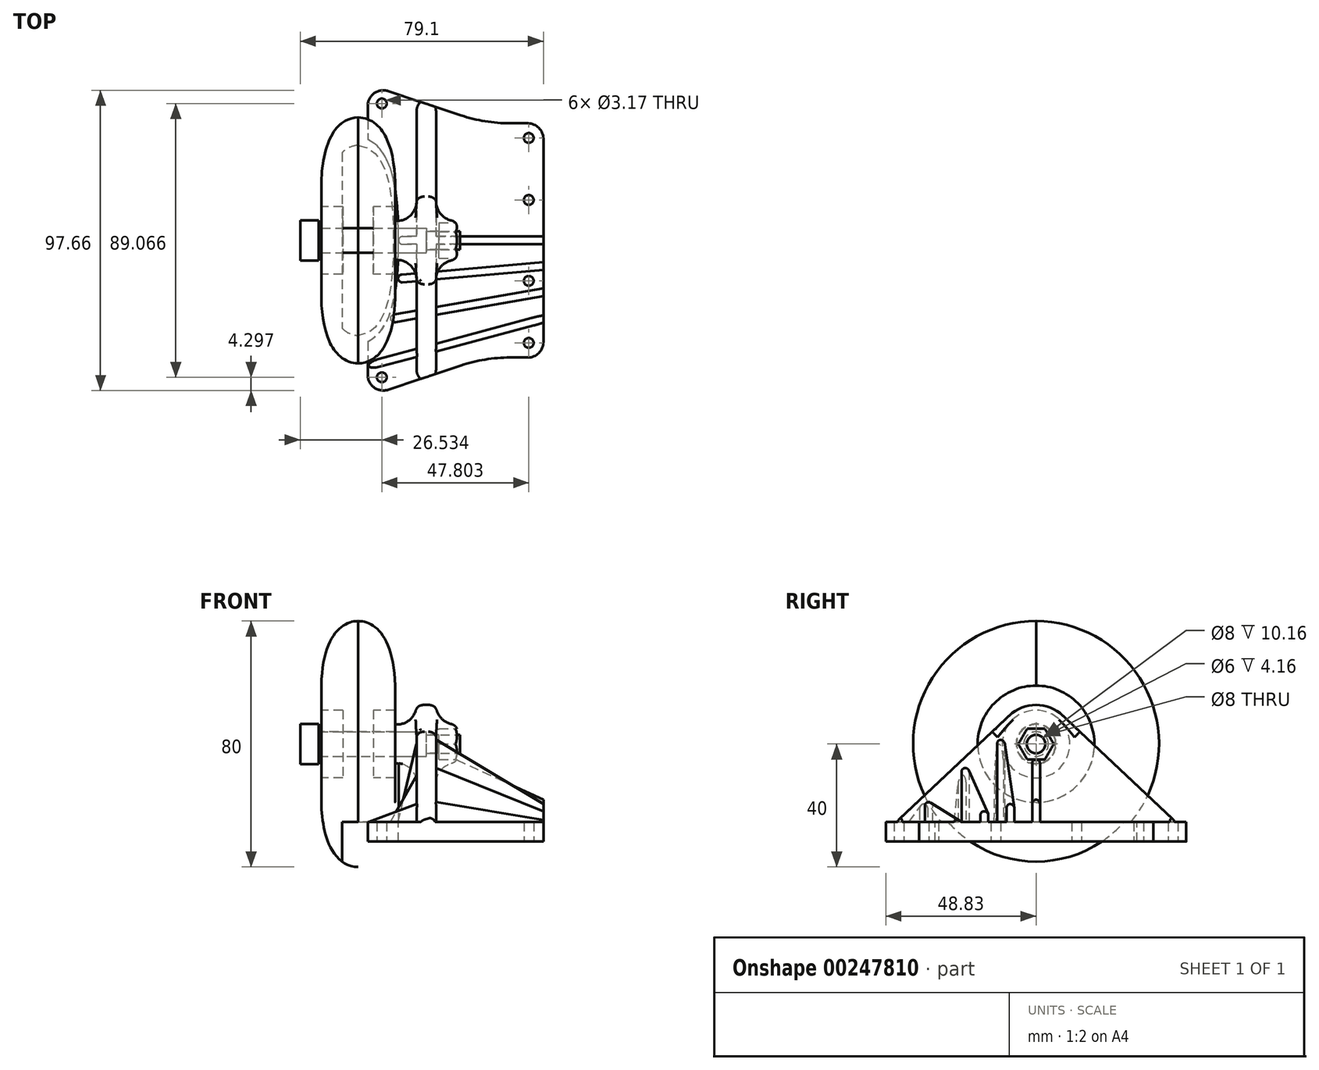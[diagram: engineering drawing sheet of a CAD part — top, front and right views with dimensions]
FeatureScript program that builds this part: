
annotation { "Feature Type Name" : "Feature", "Feature Type Description" : "" }
export const myFeature = defineFeature(function(context is Context, id is Id, definition is map)
    precondition{}
    {
        {
            var Q0;
            Q0=qCreatedBy(makeId("Top.planeOp"),FACE);
            var sketch = newSketch(context, id + "F0", { "sketchPlane" : qUnion([Q0])});
            skLineSegment(sketch, "E0", {"start": v(-19.05, 50.8) * mm, "end": v(-19.05, -50.8) * mm});
            skLineSegment(sketch, "E1", {"start": v(-19.05, -50.8) * mm, "end": v(19.05, -38.1) * mm});
            skLineSegment(sketch, "E2", {"start": v(38.1, -31.75) * mm, "end": v(38.1, 31.75) * mm});
            skLineSegment(sketch, "E3", {"start": v(19.05, 38.1) * mm, "end": v(-19.05, 50.8) * mm});
            skLineSegment(sketch, "E4", {"start": v(19.05, 38.1) * mm, "end": v(38.1, 38.1) * mm});
            skLineSegment(sketch, "E5", {"start": v(38.1, 38.1) * mm, "end": v(38.1, 31.75) * mm});
            skLineSegment(sketch, "E6", {"start": v(19.05, -38.1) * mm, "end": v(38.1, -38.1) * mm});
            skLineSegment(sketch, "E7", {"start": v(38.1, -38.1) * mm, "end": v(38.1, -31.75) * mm});
            skSolve(sketch);
        }
        {
            var Q0;
            Q0=makeQuery(id+"F0.imprint","IMPRINT",FACE,{"disambiguationData":[TD([[makeQuery(id+"F0.imprint","IMPRINT",EDGE,{"derivedFrom":sQuery(id+"F0.wireOp",EDGE,"E0")}),1.0]])]});
            extrude(context, id + "F1", {"entities" : qUnion([Q0]), "depth" : 6.35 * mm});
        }
        {
            var Q0;
            Q0=makeQuery(id+"F1.opExtrude","CAP_FACE",FACE,{"disambiguationData":[OSD([sQuery(id+"F0.wireOp",EDGE,"E0"),sQuery(id+"F0.wireOp",EDGE,"E1"),sQuery(id+"F0.wireOp",EDGE,"E2"),sQuery(id+"F0.wireOp",EDGE,"E3")])],"isStart":false});
            var sketch = newSketch(context, id + "F2", { "sketchPlane" : qUnion([Q0])});
            skLineSegment(sketch, "E8", {"start": v(-3.18, 45.5) * mm, "end": v(-3.17, -45.5) * mm});
            skLineSegment(sketch, "E9", {"start": v(-3.17, -45.5) * mm, "end": v(3.18, -43.4) * mm});
            skLineSegment(sketch, "E10", {"start": v(3.18, -43.4) * mm, "end": v(3.17, 43.4) * mm});
            skLineSegment(sketch, "E11", {"start": v(3.17, 43.4) * mm, "end": v(-3.18, 45.5) * mm});
            skSolve(sketch);
        }
        {
            var Q0;
            Q0=makeQuery(id+"F2.imprint","IMPRINT",FACE,{"disambiguationData":[TD([[makeQuery(id+"F2.imprint","IMPRINT",EDGE,{"derivedFrom":sQuery(id+"F2.wireOp",EDGE,"E8")}),1.0]])]});
            extrude(context, id + "F3", {"entities" : qUnion([Q0]), "operationType" : NewBodyOperationType.ADD, "depth" : 38.1 * mm});
        }
        {
            var Q0;
            Q0=qCreatedBy(makeId("Right.planeOp"),FACE);
            var sketch = newSketch(context, id + "F4", { "sketchPlane" : qUnion([Q0])});
            skArc(sketch, "E12", {"start": v(8.7, 41) * mm, "mid": v(0, 44.45) * mm, "end": v(-8.7, 41) * mm});
            skLineSegment(sketch, "E13", {"start": v(8.7, 41) * mm, "end": v(45.5, 6.35) * mm});
            skLineSegment(sketch, "E14", {"start": v(-8.7, 41) * mm, "end": v(-45.5, 6.35) * mm});
            skLineSegment(sketch, "E15", {"start": v(45.5, 6.35) * mm, "end": v(53.44, 6.35) * mm});
            skLineSegment(sketch, "E16", {"start": v(53.44, 6.35) * mm, "end": v(53.44, 49.76) * mm});
            skLineSegment(sketch, "E17", {"start": v(53.44, 49.76) * mm, "end": v(-55.67, 49.76) * mm});
            skLineSegment(sketch, "E18", {"start": v(-55.67, 49.76) * mm, "end": v(-55.67, 6.35) * mm});
            skLineSegment(sketch, "E19", {"start": v(-55.67, 6.35) * mm, "end": v(-45.5, 6.35) * mm});
            skSolve(sketch);
        }
        {
            var Q0;
            Q0=makeQuery(id+"F4.imprint","IMPRINT",FACE,{"disambiguationData":[TD([[makeQuery(id+"F4.imprint","IMPRINT",EDGE,{"derivedFrom":sQuery(id+"F4.wireOp",EDGE,"E12")}),-1.0]])]});
            extrude(context, id + "F5", {"entities" : qUnion([Q0]), "operationType" : NewBodyOperationType.REMOVE, "oppositeDirection" : true, "depth" : 7.11 * mm, "hasSecondDirection" : true, "secondDirectionOppositeDirection" : false, "secondDirectionDepth" : 4.06 * mm});
        }
        {
            var Q0;
            Q0=qCreatedBy(makeId("Right.planeOp"),FACE);
            var sketch = newSketch(context, id + "F6", { "sketchPlane" : qUnion([Q0])});
            skCircle(sketch, "E20", {"center": v(0, 513) * mm, "radius": 63.5 * mm});
            skCircle(sketch, "E21", {"center": v(0, 31.75) * mm, "radius": 6.35 * mm});
            skSolve(sketch);
        }
        {
            var Q0;
            Q0 = qSketchRegion(id + "F6", true);
            extrude(context, id + "F7", {"entities" : qUnion([Q0]), "operationType" : NewBodyOperationType.ADD, "depth" : 10.16 * mm, "hasSecondDirection" : true, "secondDirectionOppositeDirection" : true, "secondDirectionDepth" : 10.16 * mm});
        }
        {
            var Q0;
            Q0=makeQuery(id+"F7.boolean.opBoolean","INTERSECT",EDGE,{"derivedFrom":[makeQuery(id+"F3.opExtrude","SWEPT_FACE",FACE,{"disambiguationData":[OSD([sQuery(id+"F2.wireOp",EDGE,"E8")])]}),makeQuery(id+"F7.opExtrude","SWEPT_FACE",FACE,{"disambiguationData":[OSD([sQuery(id+"F6.wireOp",EDGE,"E21")])]})]});
            var Q1;
            Q1=makeQuery(id+"F7.boolean.opBoolean","INTERSECT",EDGE,{"derivedFrom":[makeQuery(id+"F3.opExtrude","SWEPT_FACE",FACE,{"disambiguationData":[OSD([sQuery(id+"F2.wireOp",EDGE,"E10")])]}),makeQuery(id+"F7.opExtrude","SWEPT_FACE",FACE,{"disambiguationData":[OSD([sQuery(id+"F6.wireOp",EDGE,"E21")])]})]});
            fillet(context, id + "F8", {"entities" : qUnion([Q0, Q1]), "radius" : 6.35 * mm, "tangentPropagation" : true, "allowEdgeOverflow" : false});
        }
        {
            var Q0;
            Q0=makeQuery(id+"F5.boolean.opBoolean","INTERSECT",EDGE,{"derivedFrom":[makeQuery(id+"F3.opExtrude","SWEPT_FACE",FACE,{"disambiguationData":[OSD([sQuery(id+"F2.wireOp",EDGE,"E8")])]}),makeQuery(id+"F5.opExtrude","SWEPT_FACE",FACE,{"disambiguationData":[OSD([sQuery(id+"F4.wireOp",EDGE,"E13")])]})]});
            var Q1;
            Q1=makeQuery(id+"F5.boolean.opBoolean","INTERSECT",EDGE,{"derivedFrom":[makeQuery(id+"F3.opExtrude","SWEPT_FACE",FACE,{"disambiguationData":[OSD([sQuery(id+"F2.wireOp",EDGE,"E10")])]}),makeQuery(id+"F5.opExtrude","SWEPT_FACE",FACE,{"disambiguationData":[OSD([sQuery(id+"F4.wireOp",EDGE,"E13")])]})]});
            fillet(context, id + "F9", {"entities" : qUnion([Q0, Q1]), "radius" : 2.54 * mm, "tangentPropagation" : true, "allowEdgeOverflow" : false});
        }
        {
            var Q0;
            Q0=qCreatedBy(makeId("Right.planeOp"),FACE);
            var sketch = newSketch(context, id + "F10", { "sketchPlane" : qUnion([Q0])});
            skCircle(sketch, "E22", {"center": v(0, 31.75) * mm, "radius": 4 * mm});
            skSolve(sketch);
        }
        {
            var Q0;
            Q0 = qSketchRegion(id + "F10", true);
            extrude(context, id + "F11", {"entities" : qUnion([Q0]), "operationType" : NewBodyOperationType.REMOVE, "oppositeDirection" : true, "depth" : 25.4 * mm});
        }
        {
            var Q0;
            Q0=makeQuery(id+"F7.opExtrude","CAP_FACE",FACE,{"disambiguationData":[OSD([sQuery(id+"F6.wireOp",EDGE,"E21")])],"isStart":false});
            var sketch = newSketch(context, id + "F12", { "sketchPlane" : qUnion([Q0])});
            skCircle(sketch, "E23.cCircle", {"center": v(0, 31.75) * mm, "radius": 5 * mm, "construction": true});
            skLineSegment(sketch, "E23.0", {"start": v(-2.89, 36.75) * mm, "end": v(2.89, 36.75) * mm});
            skLineSegment(sketch, "E23.1", {"start": v(2.89, 36.75) * mm, "end": v(5.77, 31.75) * mm});
            skLineSegment(sketch, "E23.2", {"start": v(5.77, 31.75) * mm, "end": v(2.89, 26.75) * mm});
            skLineSegment(sketch, "E23.3", {"start": v(2.89, 26.75) * mm, "end": v(-2.89, 26.75) * mm});
            skLineSegment(sketch, "E23.4", {"start": v(-2.89, 26.75) * mm, "end": v(-5.77, 31.75) * mm});
            skLineSegment(sketch, "E23.5", {"start": v(-5.77, 31.75) * mm, "end": v(-2.89, 36.75) * mm});
            skPoint(sketch, "E23.0.midPoint", {"position": v(0, 36.75) * mm});
            skSolve(sketch);
        }
        {
            var Q0;
            Q0=makeQuery(id+"F12.imprint","IMPRINT",FACE,{"disambiguationData":[TD([[makeQuery(id+"F12.imprint","IMPRINT",EDGE,{"derivedFrom":sQuery(id+"F12.wireOp",EDGE,"E23.0")}),-1.0]])]});
            extrude(context, id + "F13", {"entities" : qUnion([Q0]), "operationType" : NewBodyOperationType.REMOVE, "oppositeDirection" : true, "depth" : 6 * mm});
        }
        {
            var Q0;
            Q0=makeQuery(id+"F7.opExtrude","CAP_EDGE",EDGE,{"disambiguationData":[OSD([sQuery(id+"F6.wireOp",EDGE,"E21")])],"isStart":false});
            fillet(context, id + "F14", {"entities" : qUnion([Q0]), "radius" : 2.54 * mm, "tangentPropagation" : true, "allowEdgeOverflow" : false});
        }
        {
            var Q0;
            Q0=makeQuery(id+"F7.opExtrude","SWEPT_BODY",BODY,{"disambiguationData":[OSD([sQuery(id+"F6.wireOp",EDGE,"E20")])]});
            deleteBodies(context, id + "F15", {"entities" : qUnion([Q0])});
        }
        {
            var Q0;
            Q0=qCreatedBy(makeId("Right.planeOp"),FACE);
            var sketch = newSketch(context, id + "F16", { "sketchPlane" : qUnion([Q0])});
            skCircle(sketch, "E24", {"center": v(0, 31.75) * mm, "radius": 3 * mm});
            skSolve(sketch);
        }
        {
            var Q0;
            Q0 = qSketchRegion(id + "F16", true);
            extrude(context, id + "F17", {"entities" : qUnion([Q0]), "operationType" : NewBodyOperationType.REMOVE, "depth" : 25.4 * mm});
        }
        {
            var Q0;
            Q0=qCreatedBy(makeId("Front.planeOp"),FACE);
            var sketch = newSketch(context, id + "F18", { "sketchPlane" : qUnion([Q0])});
            skLineSegment(sketch, "E25", {"start": v(0, 31.75) * mm, "end": v(-46.53, 31.75) * mm, "construction": true});
            skLineSegment(sketch, "E26", {"start": v(-35, 35.75) * mm, "end": v(0, 35.75) * mm});
            skLineSegment(sketch, "E27", {"start": v(0, 35.75) * mm, "end": v(0, 34.75) * mm});
            skLineSegment(sketch, "E28", {"start": v(0, 34.75) * mm, "end": v(11, 34.75) * mm});
            skLineSegment(sketch, "E29", {"start": v(11, 34.75) * mm, "end": v(11, 31.75) * mm});
            skLineSegment(sketch, "E30", {"start": v(11, 31.75) * mm, "end": v(-41, 31.75) * mm});
            skLineSegment(sketch, "E31", {"start": v(-35, 35.75) * mm, "end": v(-35, 38.25) * mm});
            skLineSegment(sketch, "E32", {"start": v(-35, 38.25) * mm, "end": v(-41, 38.25) * mm});
            skLineSegment(sketch, "E33", {"start": v(-41, 38.25) * mm, "end": v(-41, 31.75) * mm});
            skSolve(sketch);
        }
        {
            var Q0;
            Q0=makeQuery(id+"F18.imprint","IMPRINT",FACE,{"disambiguationData":[TD([[makeQuery(id+"F18.imprint","IMPRINT",EDGE,{"derivedFrom":sQuery(id+"F18.wireOp",EDGE,"E26")}),-1.0]])]});
            var Q1;
            Q1=sQuery(id+"F18.wireOp",EDGE,"E25");
            revolve(context, id + "F19", {"entities" : qUnion([Q0]), "axis" : qUnion([Q1]), "revolveType" : RevolveType.FULL});
        }
        {
            var Q0;
            Q0=qCreatedBy(makeId("Front.planeOp"),FACE);
            var sketch = newSketch(context, id + "F20", { "sketchPlane" : qUnion([Q0])});
            skLineSegment(sketch, "E34", {"start": v(-51.26, 31.75) * mm, "end": v(0, 31.75) * mm});
            skLineSegment(sketch, "E35", {"start": v(-22.16, 31.75) * mm, "end": v(-22.16, 71.75) * mm, "construction": true});
            skPoint(sketch, "E36", {"position": v(-25.63, 31.75) * mm});
            skLineSegment(sketch, "E37", {"start": v(-22.16, 35.75) * mm, "end": v(-10.16, 35.75) * mm});
            skLineSegment(sketch, "E38", {"start": v(-10.16, 35.75) * mm, "end": v(-10.16, 50.75) * mm});
            skPoint(sketch, "E39.MirrorCS.2.internal.orphan", {"position": v(-34.16, 31.75) * mm});
            skPoint(sketch, "E39.MirrorCS.start.orphan", {"position": v(-22.16, 71.75) * mm});
            skPoint(sketch, "E40.2.internal.orphan", {"position": v(-10.16, 31.75) * mm});
            skFitSpline(sketch, "E41", {"points": [v(-22.16, 71.75) * mm, v(-10.16, 50.75) * mm], "startDerivative": vector(15.26, -0.07) * mm, "endDerivative": vector(1.21, -49.43) * mm});
            skPoint(sketch, "E42.MirrorCS.end.orphan", {"position": v(-34.16, 50.75) * mm});
            skFitSpline(sketch, "E43.MirrorCS", {"points": [v(-22.16, 71.75) * mm, v(-34.16, 50.75) * mm], "startDerivative": vector(-15.26, -0.07) * mm, "endDerivative": vector(-1.21, -49.43) * mm});
            skLineSegment(sketch, "E44.MirrorCS", {"start": v(-34.16, 35.75) * mm, "end": v(-34.16, 50.75) * mm});
            skLineSegment(sketch, "E45.MirrorCS", {"start": v(-22.16, 35.75) * mm, "end": v(-34.16, 35.75) * mm});
            skSolve(sketch);
        }
        {
            var Q0;
            Q0=makeQuery(id+"F20.imprint","IMPRINT",FACE,{"disambiguationData":[TD([[makeQuery(id+"F20.imprint","IMPRINT",EDGE,{"derivedFrom":sQuery(id+"F20.wireOp",EDGE,"E37")}),1.0]])]});
            var Q1;
            Q1=sQuery(id+"F20.wireOp",EDGE,"E34");
            revolve(context, id + "F21", {"entities" : qUnion([Q0]), "axis" : qUnion([Q1]), "revolveType" : RevolveType.FULL});
        }
        {
            var Q0;
            Q0=qCreatedBy(makeId("Front.planeOp"),FACE);
            var sketch = newSketch(context, id + "F22", { "sketchPlane" : qUnion([Q0])});
            skLineSegment(sketch, "E46", {"start": v(-62.06, 31.75) * mm, "end": v(0, 31.75) * mm, "construction": true});
            skLineSegment(sketch, "E47", {"start": v(-10.16, 31.75) * mm, "end": v(-10.16, 42.75) * mm});
            skLineSegment(sketch, "E48", {"start": v(-10.16, 42.75) * mm, "end": v(-17.16, 42.75) * mm});
            skLineSegment(sketch, "E49", {"start": v(-17.16, 42.75) * mm, "end": v(-17.16, 31.75) * mm});
            skLineSegment(sketch, "E50", {"start": v(-17.16, 31.75) * mm, "end": v(-10.16, 31.75) * mm});
            skLineSegment(sketch, "E51", {"start": v(-22.16, 31.75) * mm, "end": v(-22.16, 46.12) * mm, "construction": true});
            skLineSegment(sketch, "E52.MirrorCS", {"start": v(-34.16, 42.75) * mm, "end": v(-27.16, 42.75) * mm});
            skLineSegment(sketch, "E53.MirrorCS", {"start": v(-27.16, 42.75) * mm, "end": v(-27.16, 31.75) * mm});
            skLineSegment(sketch, "E54.MirrorCS", {"start": v(-34.16, 31.75) * mm, "end": v(-34.16, 42.75) * mm});
            skLineSegment(sketch, "E55", {"start": v(-27.16, 31.75) * mm, "end": v(-34.16, 31.75) * mm});
            skSolve(sketch);
        }
        {
            var Q0;
            Q0 = qSketchRegion(id + "F22", true);
            var Q1;
            Q1=sQuery(id+"F22.wireOp",EDGE,"E46");
            revolve(context, id + "F23", {"entities" : qUnion([Q0]), "axis" : qUnion([Q1]), "revolveType" : RevolveType.FULL});
        }
        {
            var Q0;
            {var subQ0=sQuery(id+"F0.wireOp",EDGE,"E3");var subQ1=sQuery(id+"F0.wireOp",EDGE,"E1");var subQ2=sQuery(id+"F0.wireOp",EDGE,"E0");Q0=makeQuery(id+"F3.boolean.opBoolean","SPLIT",FACE,{"disambiguationData":[TD([makeQuery(id+"F1.opExtrude","SWEPT_FACE",FACE,{"disambiguationData":[OSD([subQ2])]})])],"derivedFrom":makeQuery(id+"F1.opExtrude","CAP_FACE",FACE,{"disambiguationData":[OSD([subQ2,subQ1,sQuery(id+"F0.wireOp",EDGE,"E2"),subQ0])],"isStart":false})});}
            var sketch = newSketch(context, id + "F24", { "sketchPlane" : qUnion([Q0])});
            skLineSegment(sketch, "E56", {"start": v(-19.05, 32.85) * mm, "end": v(-19.05, -32.85) * mm});
            skFitSpline(sketch, "E57.0", {"points": [v(-22.67, -33.39) * mm, v(-22.46, -33.43) * mm, v(-22.05, -33.49) * mm, v(-21.48, -33.49) * mm, v(-20.97, -33.44) * mm, v(-20.5, -33.35) * mm, v(-20.07, -33.24) * mm, v(-19.65, -33.1) * mm, v(-19.27, -32.95) * mm, v(-18.9, -32.79) * mm, v(-18.56, -32.62) * mm, v(-18.23, -32.43) * mm, v(-17.91, -32.24) * mm, v(-17.5, -31.97) * mm, v(-17.03, -31.62) * mm, v(-16.3, -31.03) * mm, v(-15.49, -30.22) * mm, v(-14.62, -29.2) * mm, v(-13.87, -28.1) * mm, v(-13.21, -26.98) * mm, v(-12.65, -25.84) * mm, v(-12.17, -24.7) * mm, v(-11.76, -23.55) * mm, v(-11.28, -22.02) * mm, v(-10.8, -20.12) * mm, v(-10.34, -17.83) * mm, v(-10, -15.56) * mm, v(-9.63, -12.57) * mm, v(-9.33, -8.85) * mm, v(-9.13, -4.4) * mm, v(-9.07, 0.02) * mm, v(-9.13, 4.46) * mm, v(-9.3, 8.17) * mm, v(-9.52, 11.16) * mm, v(-9.73, 13.4) * mm, v(-10, 15.66) * mm, v(-10.36, 17.92) * mm, v(-10.81, 20.2) * mm, v(-11.4, 22.47) * mm, v(-12.03, 24.37) * mm, v(-12.67, 25.89) * mm, v(-13.24, 27.03) * mm, v(-13.9, 28.15) * mm, v(-14.65, 29.23) * mm, v(-15.52, 30.26) * mm, v(-16.5, 31.2) * mm, v(-17.6, 32.06) * mm, v(-18.66, 32.7) * mm, v(-19.65, 33.11) * mm, v(-20.35, 33.32) * mm, v(-20.98, 33.44) * mm, v(-21.49, 33.49) * mm, v(-22.05, 33.48) * mm, v(-22.46, 33.43) * mm, v(-22.67, 33.39) * mm]});
            skPoint(sketch, "E58.trimOffspring.end.orphan", {"position": v(-22.16, 30.9) * mm});
            skPoint(sketch, "E59.start.orphan", {"position": v(-22.16, -30.9) * mm});
            skLineSegment(sketch, "E60", {"start": v(-19.05, 32.85) * mm, "end": v(-27.36, 32.85) * mm});
            skLineSegment(sketch, "E61", {"start": v(-27.36, 32.85) * mm, "end": v(-27.36, -33.81) * mm});
            skLineSegment(sketch, "E62", {"start": v(-27.36, -33.81) * mm, "end": v(-19.05, -32.85) * mm});
            skSolve(sketch);
        }
        {
            var Q0;
            Q0=makeQuery(id+"F24.imprint","IMPRINT",FACE,{"disambiguationData":[TD([[makeQuery(id+"F24.imprint","IMPRINT",EDGE,{"derivedFrom":sQuery(id+"F24.wireOp",EDGE,"E56")}),-1.0]])]});
            var Q1;
            Q1=makeQuery(id+"F24.imprint","IMPRINT",FACE,{"disambiguationData":[TD([[makeQuery(id+"F24.imprint","IMPRINT",EDGE,{"derivedFrom":sQuery(id+"F24.wireOp",EDGE,"E56")}),1.0]])]});
            extrude(context, id + "F25", {"entities" : qUnion([Q0, Q1]), "operationType" : NewBodyOperationType.REMOVE, "oppositeDirection" : true, "depth" : 25.4 * mm});
        }
        {
            var Q0;
            Q0=qCreatedBy(makeId("Front.planeOp"),FACE);
            var sketch = newSketch(context, id + "F26", { "sketchPlane" : qUnion([Q0])});
            skLineSegment(sketch, "E63", {"start": v(-9.01, 6.35) * mm, "end": v(-9.01, 26.67) * mm});
            skLineSegment(sketch, "E64", {"start": v(-9.01, 26.67) * mm, "end": v(9.85, 26.67) * mm});
            skLineSegment(sketch, "E65", {"start": v(9.85, 26.67) * mm, "end": v(53.98, 6.35) * mm});
            skLineSegment(sketch, "E66", {"start": v(53.98, 6.35) * mm, "end": v(-9.01, 6.35) * mm});
            skSolve(sketch);
        }
        {
            var Q0;
            Q0=makeQuery(id+"F26.imprint","IMPRINT",FACE,{"disambiguationData":[TD([[makeQuery(id+"F26.imprint","IMPRINT",EDGE,{"derivedFrom":sQuery(id+"F26.wireOp",EDGE,"E63")}),-1.0]])]});
            extrude(context, id + "F27", {"entities" : qUnion([Q0]), "operationType" : NewBodyOperationType.ADD, "depth" : 1.27 * mm, "hasSecondDirection" : true, "secondDirectionOppositeDirection" : true, "secondDirectionDepth" : 1.27 * mm});
        }
        {
            var Q0;
            Q0=qCreatedBy(makeId("Top.planeOp"),FACE);
            var sketch = newSketch(context, id + "F28", { "sketchPlane" : qUnion([Q0])});
            skLineSegment(sketch, "E67", {"start": v(-23.06, -52.14) * mm, "end": v(133.35, 0) * mm});
            skLineSegment(sketch, "E68", {"start": v(133.35, 0) * mm, "end": v(-28.84, 0) * mm});
            skLineSegment(sketch, "E69", {"start": v(133.35, 0) * mm, "end": v(-37.86, -14.98) * mm});
            skLineSegment(sketch, "E70", {"start": v(133.35, 0) * mm, "end": v(-37.54, -30.13) * mm});
            skLineSegment(sketch, "E71", {"start": v(133.35, 0) * mm, "end": v(-45.99, -48.05) * mm});
            skSolve(sketch);
        }
        {
            var Q0;
            Q0=sQuery(id+"F28.wireOp",EDGE,"E69");
            cPlane(context, id + "F29", {"entities" : qUnion([Q0]), "cplaneType" : CPlaneType.LINE_ANGLE, "offset" : 25.4 * mm, "angle" : 0 * degree, "width" : 152.4 * mm, "height" : 152.4 * mm});
        }
        {
            var Q0;
            Q0=qCreatedBy(id+"F29.planeOp",FACE);
            var sketch = newSketch(context, id + "F30", { "sketchPlane" : qUnion([Q0])});
            skLineSegment(sketch, "E72", {"start": v(0, 34.47) * mm, "end": v(47.09, 6.35) * mm});
            skLineSegment(sketch, "E73", {"start": v(47.09, 6.35) * mm, "end": v(-10.24, 6.35) * mm});
            skLineSegment(sketch, "E74", {"start": v(-3.1, 36.6) * mm, "end": v(0, 34.47) * mm});
            skLineSegment(sketch, "E75", {"start": v(-10.24, 6.35) * mm, "end": v(-3.1, 36.6) * mm});
            skSolve(sketch);
        }
        {
            var Q0;
            Q0=makeQuery(id+"F30.imprint","IMPRINT",FACE,{"disambiguationData":[TD([[makeQuery(id+"F30.imprint","IMPRINT",EDGE,{"derivedFrom":sQuery(id+"F30.wireOp",EDGE,"E72")}),-1.0]])]});
            extrude(context, id + "F31", {"entities" : qUnion([Q0]), "operationType" : NewBodyOperationType.ADD, "depth" : 1.27 * mm, "hasSecondDirection" : true, "secondDirectionOppositeDirection" : true, "secondDirectionDepth" : 1.27 * mm});
        }
        {
            var Q0;
            Q0=sQuery(id+"F28.wireOp",EDGE,"E70");
            cPlane(context, id + "F32", {"entities" : qUnion([Q0]), "cplaneType" : CPlaneType.LINE_ANGLE, "offset" : 25.4 * mm, "angle" : 0 * degree, "width" : 152.4 * mm, "height" : 152.4 * mm});
        }
        {
            var Q0;
            Q0=qCreatedBy(id+"F32.planeOp",FACE);
            var sketch = newSketch(context, id + "F33", { "sketchPlane" : qUnion([Q0])});
            skLineSegment(sketch, "E76", {"start": v(43.53, 6.35) * mm, "end": v(-15.92, 6.35) * mm});
            skLineSegment(sketch, "E77", {"start": v(-15.92, 6.35) * mm, "end": v(-5.38, 24.92) * mm});
            skLineSegment(sketch, "E78", {"start": v(-5.38, 24.92) * mm, "end": v(-3.33, 24.92) * mm});
            skLineSegment(sketch, "E79", {"start": v(-3.33, 24.92) * mm, "end": v(43.53, 6.35) * mm});
            skSolve(sketch);
        }
        {
            var Q0;
            Q0=makeQuery(id+"F33.imprint","IMPRINT",FACE,{"disambiguationData":[TD([[makeQuery(id+"F33.imprint","IMPRINT",EDGE,{"derivedFrom":sQuery(id+"F33.wireOp",EDGE,"E76")}),-1.0]])]});
            extrude(context, id + "F34", {"entities" : qUnion([Q0]), "operationType" : NewBodyOperationType.ADD, "depth" : 1.27 * mm, "hasSecondDirection" : true, "secondDirectionOppositeDirection" : true, "secondDirectionDepth" : 1.27 * mm});
        }
        {
            var Q0;
            Q0=sQuery(id+"F28.wireOp",EDGE,"E71");
            cPlane(context, id + "F35", {"entities" : qUnion([Q0]), "cplaneType" : CPlaneType.LINE_ANGLE, "offset" : 25.4 * mm, "angle" : 0 * degree, "width" : 152.4 * mm, "height" : 152.4 * mm});
        }
        {
            var Q0;
            Q0=qCreatedBy(id+"F35.planeOp",FACE);
            var sketch = newSketch(context, id + "F36", { "sketchPlane" : qUnion([Q0])});
            skLineSegment(sketch, "E80", {"start": v(-28.7, 6.35) * mm, "end": v(-10.05, 13.08) * mm});
            skLineSegment(sketch, "E81", {"start": v(-10.05, 13.08) * mm, "end": v(-7.43, 13.08) * mm});
            skLineSegment(sketch, "E82", {"start": v(-7.43, 13.08) * mm, "end": v(34.6, 6.35) * mm});
            skLineSegment(sketch, "E83", {"start": v(34.6, 6.35) * mm, "end": v(-28.7, 6.35) * mm});
            skSolve(sketch);
        }
        {
            var Q0;
            Q0=makeQuery(id+"F36.imprint","IMPRINT",FACE,{"disambiguationData":[TD([[makeQuery(id+"F36.imprint","IMPRINT",EDGE,{"derivedFrom":sQuery(id+"F36.wireOp",EDGE,"E80")}),-1.0]])]});
            extrude(context, id + "F37", {"entities" : qUnion([Q0]), "operationType" : NewBodyOperationType.ADD, "depth" : 1.27 * mm, "hasSecondDirection" : true, "secondDirectionOppositeDirection" : true, "secondDirectionDepth" : 1.27 * mm});
        }
        {
            var Q0;
            Q0=qCreatedBy(makeId("Top.planeOp"),FACE);
            var sketch = newSketch(context, id + "F38", { "sketchPlane" : qUnion([Q0])});
            skLineSegment(sketch, "E84", {"start": v(-19.05, 47.14) * mm, "end": v(-19.05, -47.14) * mm});
            skLineSegment(sketch, "E85", {"start": v(-12.36, 48.57) * mm, "end": v(-22.52, 51.96) * mm});
            skLineSegment(sketch, "E86", {"start": v(38.1, 70.87) * mm, "end": v(38.1, -40.92) * mm});
            skLineSegment(sketch, "E87", {"start": v(-22.52, -51.96) * mm, "end": v(-12.36, -48.57) * mm});
            skPoint(sketch, "E88.visualSharp", {"position": v(-19.05, 50.8) * mm});
            skArc(sketch, "E88.filletArc", {"start": v(-19.05, 47.14) * mm, "mid": v(-20, 50.1) * mm, "end": v(-22.52, 51.96) * mm});
            skPoint(sketch, "E89.visualSharp", {"position": v(-19.05, -50.8) * mm});
            skArc(sketch, "E89.filletArc", {"start": v(-22.52, -51.96) * mm, "mid": v(-20, -50.1) * mm, "end": v(-19.05, -47.14) * mm});
            skLineSegment(sketch, "E90", {"start": v(-19.05, 43.75) * mm, "end": v(-19.05, 35.1) * mm});
            skLineSegment(sketch, "E91", {"start": v(-19.05, 35.1) * mm, "end": v(-54.33, 35.1) * mm});
            skLineSegment(sketch, "E92", {"start": v(-54.33, 35.1) * mm, "end": v(-54.33, 78.4) * mm});
            skLineSegment(sketch, "E93", {"start": v(-54.33, 78.4) * mm, "end": v(38.1, 70.87) * mm});
            skArc(sketch, "E94.filletArc", {"start": v(-12.36, 48.57) * mm, "mid": v(-16.94, 47.87) * mm, "end": v(-19.05, 43.75) * mm});
            skLineSegment(sketch, "E95", {"start": v(-19.05, -43.75) * mm, "end": v(-19.05, -36.43) * mm});
            skLineSegment(sketch, "E96", {"start": v(-19.05, -36.43) * mm, "end": v(-56.87, -36.43) * mm});
            skLineSegment(sketch, "E97", {"start": v(-56.87, -36.43) * mm, "end": v(-56.87, -71.2) * mm});
            skLineSegment(sketch, "E98", {"start": v(-56.87, -71.2) * mm, "end": v(38.1, -40.92) * mm});
            skArc(sketch, "E99.filletArc", {"start": v(-19.05, -43.75) * mm, "mid": v(-16.94, -47.87) * mm, "end": v(-12.36, -48.57) * mm});
            skSolve(sketch);
        }
        {
            var Q0;
            Q0=makeQuery(id+"F38.imprint","IMPRINT",FACE,{"disambiguationData":[TD([[makeQuery(id+"F38.imprint","IMPRINT",EDGE,{"derivedFrom":sQuery(id+"F38.wireOp",EDGE,"E84")}),1.0]])]});
            extrude(context, id + "F39", {"entities" : qUnion([Q0]), "operationType" : NewBodyOperationType.REMOVE, "depth" : 25.4 * mm});
        }
        {
            var Q0;
            Q0=makeQuery(id+"F37.opExtrude","CAP_EDGE",EDGE,{"disambiguationData":[OSD([sQuery(id+"F36.wireOp",EDGE,"E82")])],"isStart":false});
            var Q1;
            Q1=makeQuery(id+"F37.opExtrude","CAP_EDGE",EDGE,{"disambiguationData":[OSD([sQuery(id+"F36.wireOp",EDGE,"E82")])],"isStart":true});
            var Q2;
            Q2=makeQuery(id+"F34.opExtrude","CAP_EDGE",EDGE,{"disambiguationData":[OSD([sQuery(id+"F33.wireOp",EDGE,"E79")])],"isStart":false});
            var Q3;
            Q3=makeQuery(id+"F34.opExtrude","CAP_EDGE",EDGE,{"disambiguationData":[OSD([sQuery(id+"F33.wireOp",EDGE,"E79")])],"isStart":true});
            var Q4;
            Q4=makeQuery(id+"F31.opExtrude","CAP_EDGE",EDGE,{"disambiguationData":[OSD([sQuery(id+"F30.wireOp",EDGE,"E72")])],"isStart":false});
            var Q5;
            Q5=makeQuery(id+"F31.opExtrude","CAP_EDGE",EDGE,{"disambiguationData":[OSD([sQuery(id+"F30.wireOp",EDGE,"E72")])],"isStart":true});
            var Q6;
            Q6=makeQuery(id+"F27.opExtrude","CAP_EDGE",EDGE,{"disambiguationData":[OSD([sQuery(id+"F26.wireOp",EDGE,"E65")])],"isStart":false});
            var Q7;
            Q7=makeQuery(id+"F27.opExtrude","CAP_EDGE",EDGE,{"disambiguationData":[OSD([sQuery(id+"F26.wireOp",EDGE,"E65")])],"isStart":true});
            var Q8;
            Q8=makeQuery(id+"FzpeDoiq8tc86xp_5.1.F31.opExtrude","CAP_EDGE",EDGE,{"disambiguationData":[OSD([sQuery(id+"F30.wireOp",EDGE,"E72")])],"isStart":true});
            var Q9;
            Q9=makeQuery(id+"FzpeDoiq8tc86xp_5.1.F31.opExtrude","CAP_EDGE",EDGE,{"disambiguationData":[OSD([sQuery(id+"F30.wireOp",EDGE,"E72")])],"isStart":false});
            var Q10;
            Q10=makeQuery(id+"FzpeDoiq8tc86xp_5.1.F34.opExtrude","CAP_EDGE",EDGE,{"disambiguationData":[OSD([sQuery(id+"F33.wireOp",EDGE,"E79")])],"isStart":true});
            var Q11;
            Q11=makeQuery(id+"FzpeDoiq8tc86xp_5.1.F34.opExtrude","CAP_EDGE",EDGE,{"disambiguationData":[OSD([sQuery(id+"F33.wireOp",EDGE,"E79")])],"isStart":false});
            var Q12;
            Q12=makeQuery(id+"FzpeDoiq8tc86xp_5.1.F37.opExtrude","CAP_EDGE",EDGE,{"disambiguationData":[OSD([sQuery(id+"F36.wireOp",EDGE,"E82")])],"isStart":true});
            var Q13;
            Q13=makeQuery(id+"F37.opExtrude","CAP_EDGE",EDGE,{"disambiguationData":[OSD([sQuery(id+"F36.wireOp",EDGE,"E80")])],"isStart":false});
            var Q14;
            Q14=makeQuery(id+"F37.opExtrude","CAP_EDGE",EDGE,{"disambiguationData":[OSD([sQuery(id+"F36.wireOp",EDGE,"E80")])],"isStart":true});
            var Q15;
            Q15=makeQuery(id+"F34.opExtrude","CAP_EDGE",EDGE,{"disambiguationData":[OSD([sQuery(id+"F33.wireOp",EDGE,"E77")])],"isStart":false});
            var Q16;
            Q16=makeQuery(id+"F34.opExtrude","CAP_EDGE",EDGE,{"disambiguationData":[OSD([sQuery(id+"F33.wireOp",EDGE,"E77")])],"isStart":true});
            var Q17;
            {var subQ0=sQuery(id+"F30.wireOp",EDGE,"E75");Q17=makeQuery(id+"F31.boolean.opBoolean","SPLIT",EDGE,{"disambiguationData":[TD([makeQuery(id+"F3.opExtrude","SWEPT_FACE",FACE,{"disambiguationData":[OSD([sQuery(id+"F2.wireOp",EDGE,"E8")])]})])],"derivedFrom":makeQuery(id+"F31.opExtrude","CAP_EDGE",EDGE,{"disambiguationData":[OSD([subQ0])],"isStart":false})});}
            var Q18;
            Q18=makeQuery(id+"F31.opExtrude","CAP_EDGE",EDGE,{"disambiguationData":[OSD([sQuery(id+"F30.wireOp",EDGE,"E75")])],"isStart":true});
            var Q19;
            Q19=makeQuery(id+"F27.opExtrude","CAP_EDGE",EDGE,{"disambiguationData":[OSD([sQuery(id+"F26.wireOp",EDGE,"E63")])],"isStart":false});
            var Q20;
            Q20=makeQuery(id+"F27.opExtrude","CAP_EDGE",EDGE,{"disambiguationData":[OSD([sQuery(id+"F26.wireOp",EDGE,"E63")])],"isStart":true});
            var Q21;
            Q21=makeQuery(id+"FzpeDoiq8tc86xp_5.1.F31.opExtrude","CAP_EDGE",EDGE,{"disambiguationData":[OSD([sQuery(id+"F30.wireOp",EDGE,"E75")])],"isStart":true});
            var Q22;
            {var subQ0=sQuery(id+"F30.wireOp",EDGE,"E75");Q22=makeQuery(id+"FzpeDoiq8tc86xp_5.1.F31.boolean.opBoolean","SPLIT",EDGE,{"disambiguationData":[TD([makeQuery(id+"F3.opExtrude","SWEPT_FACE",FACE,{"disambiguationData":[OSD([sQuery(id+"F2.wireOp",EDGE,"E8")])]})])],"derivedFrom":makeQuery(id+"FzpeDoiq8tc86xp_5.1.F31.opExtrude","CAP_EDGE",EDGE,{"disambiguationData":[OSD([subQ0])],"isStart":false})});}
            var Q23;
            Q23=makeQuery(id+"FzpeDoiq8tc86xp_5.1.F34.opExtrude","CAP_EDGE",EDGE,{"disambiguationData":[OSD([sQuery(id+"F33.wireOp",EDGE,"E77")])],"isStart":true});
            var Q24;
            Q24=makeQuery(id+"FzpeDoiq8tc86xp_5.1.F34.opExtrude","CAP_EDGE",EDGE,{"disambiguationData":[OSD([sQuery(id+"F33.wireOp",EDGE,"E77")])],"isStart":false});
            var Q25;
            Q25=makeQuery(id+"FzpeDoiq8tc86xp_5.1.F37.opExtrude","CAP_EDGE",EDGE,{"disambiguationData":[OSD([sQuery(id+"F36.wireOp",EDGE,"E80")])],"isStart":true});
            var Q26;
            Q26=makeQuery(id+"FzpeDoiq8tc86xp_5.1.F37.opExtrude","CAP_EDGE",EDGE,{"disambiguationData":[OSD([sQuery(id+"F36.wireOp",EDGE,"E80")])],"isStart":false});
            var Q27;
            Q27=makeQuery(id+"FzpeDoiq8tc86xp_5.1.F37.opExtrude","CAP_EDGE",EDGE,{"disambiguationData":[OSD([sQuery(id+"F36.wireOp",EDGE,"E82")])],"isStart":false});
            fillet(context, id + "F40", {"entities" : qUnion([Q0, Q1, Q2, Q3, Q4, Q5, Q6, Q7, Q8, Q9, Q10, Q11, Q12, Q13, Q14, Q15, Q16, Q17, Q18, Q19, Q20, Q21, Q22, Q23, Q24, Q25, Q26, Q27]), "radius" : 1.27 * mm, "tangentPropagation" : true, "allowEdgeOverflow" : false});
        }
        {
            var Q0;
            Q0=qCreatedBy(makeId("Top.planeOp"),FACE);
            var sketch = newSketch(context, id + "F41", { "sketchPlane" : qUnion([Q0])});
            skCircle(sketch, "E100", {"center": v(-14.47, 44.53) * mm, "radius": 1.59 * mm});
            skCircle(sketch, "E101", {"center": v(33.34, 33.34) * mm, "radius": 1.59 * mm});
            skCircle(sketch, "E102", {"center": v(33.34, 13.15) * mm, "radius": 1.59 * mm});
            skLineSegment(sketch, "E103", {"start": v(-47.45, 0) * mm, "end": v(55.73, 0) * mm, "construction": true});
            skCircle(sketch, "E104.MirrorC", {"center": v(-14.47, -44.53) * mm, "radius": 1.59 * mm});
            skCircle(sketch, "E105.MirrorC", {"center": v(33.34, -33.34) * mm, "radius": 1.59 * mm});
            skCircle(sketch, "E106.MirrorC", {"center": v(33.34, -13.15) * mm, "radius": 1.59 * mm});
            skSolve(sketch);
        }
        {
            var Q0;
            Q0 = qSketchRegion(id + "F41", true);
            extrude(context, id + "F42", {"entities" : qUnion([Q0]), "operationType" : NewBodyOperationType.REMOVE, "depth" : 25.4 * mm});
        }
        {
            var Q0;
            Q0=qCreatedBy(makeId("Top.planeOp"),FACE);
            var sketch = newSketch(context, id + "F43", { "sketchPlane" : qUnion([Q0])});
            skLineSegment(sketch, "E107", {"start": v(38.1, 38.22) * mm, "end": v(38.1, -45.48) * mm});
            skLineSegment(sketch, "E108", {"start": v(38.1, -45.48) * mm, "end": v(62.17, -45.48) * mm});
            skLineSegment(sketch, "E109", {"start": v(62.17, -45.48) * mm, "end": v(51.52, 37.8) * mm});
            skLineSegment(sketch, "E110", {"start": v(51.52, 37.8) * mm, "end": v(38.1, 38.22) * mm});
            skSolve(sketch);
        }
        {
            var Q0;
            Q0=makeQuery(id+"F43.imprint","IMPRINT",FACE,{"disambiguationData":[TD([[makeQuery(id+"F43.imprint","IMPRINT",EDGE,{"derivedFrom":sQuery(id+"F43.wireOp",EDGE,"E107")}),1.0]])]});
            extrude(context, id + "F44", {"entities" : qUnion([Q0]), "operationType" : NewBodyOperationType.REMOVE, "depth" : 22.35 * mm});
        }
        {
            var Q0;
            Q0=makeQuery(id+"F1.opExtrude","SWEPT_EDGE",EDGE,{"disambiguationData":[OSD([sQuery(id+"F0.wireOp",EDGE,"E6"),sQuery(id+"F0.wireOp",EDGE,"E7")])]});
            var Q1;
            Q1=makeQuery(id+"F1.opExtrude","SWEPT_EDGE",EDGE,{"disambiguationData":[OSD([sQuery(id+"F0.wireOp",EDGE,"E4"),sQuery(id+"F0.wireOp",EDGE,"E5")])]});
            fillet(context, id + "F45", {"entities" : qUnion([Q0, Q1]), "radius" : 5.08 * mm, "tangentPropagation" : true, "allowEdgeOverflow" : false});
        }
        {
            var Q0;
            Q0=makeQuery(id+"F1.opExtrude","SWEPT_EDGE",EDGE,{"disambiguationData":[OSD([sQuery(id+"F0.wireOp",EDGE,"E3"),sQuery(id+"F0.wireOp",EDGE,"E4")])]});
            var Q1;
            Q1=makeQuery(id+"F1.opExtrude","SWEPT_EDGE",EDGE,{"disambiguationData":[OSD([sQuery(id+"F0.wireOp",EDGE,"E1"),sQuery(id+"F0.wireOp",EDGE,"E6")])]});
            fillet(context, id + "F46", {"entities" : qUnion([Q0, Q1]), "radius" : 50.8 * mm, "tangentPropagation" : true, "allowEdgeOverflow" : false});
        }
    });
